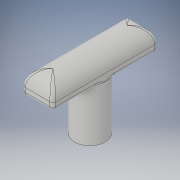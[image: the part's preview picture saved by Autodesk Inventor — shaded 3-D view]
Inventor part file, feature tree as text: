
AUTODESK INVENTOR PART (.ipt)
format: ipt  version: 2019 (Build 230136000, 136)  size: 190,976 bytes
history: native  units: mm
features: fillet x3, extrude x2, sketch x2, hole x1, thread x1
ambient origin geometry x8: Origin, YZ Plane, XZ Plane, XY Plane, X Axis, Y Axis, Z Axis, Center Point
bodies: Solid1 (feature_tree)
feature tree (9):
  extrude  "Extrusion1"  Depth=17.5mm
  extrude  "Extrusion2"  Depth=5.1mm
  fillet  "Fillet1"  [1 undecoded]
  hole  "Hole1"  [1 undecoded]
  fillet  "Fillet2"  Radius=4.2mm
  fillet  "Fillet3"  Radius=3.0mm
  thread  "Thread1"  [1 undecoded]
  sketch  "Sketch1"  dims[d1=17.5mm d2=0.0mm d3=17.5mm]
  sketch  "Sketch3"  dims[d4=7.5mm d5=0.0mm d6=5.1mm d7=135.0deg d8=5.1mm d9=4.2mm d10=3.0mm d11=45.0deg d12=4.2mm d13=6.0mm d14=4.0mm d15=2.0mm d16=90.0deg d17=8.0mm d18=20.594885mm d19=10.2mm d20=1.0mm d21=1.0mm d22=10.0mm d23=0.0mm]
note: 3 required parameter values undecoded (feature->parameter linkage not recoverable at this tier; creation-order binding heuristic only, values carry confidence <= 0.55)
